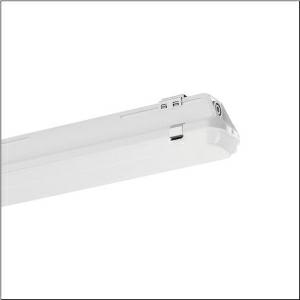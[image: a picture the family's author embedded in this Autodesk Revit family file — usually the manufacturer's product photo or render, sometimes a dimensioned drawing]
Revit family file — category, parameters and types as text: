
# Revit family: monsun_11_51fp20ep460l
name_source: partatom
category: Lighting Fixtures
units: mm (PartAtom-declared; Revit-internal decimal feet)

## family parameters
Cut with Voids When Loaded = No
Host = Face
Light Source = No
Part Type = Normal
Room Calculation Point = No
Round Connector Dimension = Use Diameter
Shared = No

## types (1)
- --- (1 x LED, 5450 lm, 31.5 W, 4000K)
    Apparent Load = 32 VA
    CIE Flux Codes = 45 75 93 94 100
    Color Rendering = 80
    Color Temperature = 4000K
    Default Elevation = 1800 mm
    Description = Monsun 11, damp-proof luminaire, chain hanger, primary optical cover: enclosure, of PC, light emission: direct distribution, primary light characteristic: symmetric, installation type: suspended mounting, surface-mounted, horizontal mounting, vertical mounting, LED, rated luminous flux: 5.450lm, luminous efficacy: 173lm/W, light colour: 840, colour temperature: 4000K, control gear: DALI 2, with terminal, 5-pole, max. 2.5mm², mains connection: 220..240V, AC, 50/60Hz, rated input power: 32W, luminaire housing, of glass-fibre reinforced polyester, uncoated, bright grey, incl. chain hanger, length: 1.590mm, width: 90mm, height: 88mm, clip for enclosure, of stainless steel (V2A), ceiling mounting element, of stainless steel (V2A), chain hanger, of stainless steel (V2A), protection rating (complete): IP66, insulation class (complete): insulation class I (protective earthing), certification: CE, ENEC, VDE, UKCA, protection symbol: D, impact resistance: IK08, permissible operating ambient temperature: -25..+35°C, standard: EN 50419, EN 60598-2-1, corresponds to IFS (International Featured Standards) requirements for safety and quality in the food industry, for indoor or canopied outdoor use, no direct snow, no direct sun, no direct rain, LABS conformity tested according to VDMA 24364:2018-05, contact your sales advisor before using the luminaires in applications with unclear chemical exposure, large temperature fluctuations or condensation-forming humidity, packaging unit: 1 piece
    Height = 89 mm
    Lamp = 1 x LED
    Lamp Light Flux = 5450 lm
    Lamp Power = 31.5 W
    Lamp count = 1
    Length = 1590 mm
    Luminous efficacy = 173 lm/W
    Manufacturer = Siteco
    ModVariant = No
    Model = 51FP20EP460L
    Mounting Place = Ceiling
    Mounting Type = Surface mounted
    Number of Poles = 1
    OnlyDefault = Yes
    Power Factor = 1
    Product Name = Monsun 11
    Product group = damp-proof luminaire
    ProductGroupID = 300
    Protection Class = Protection class I
    Protection Degree = IP 66
    RLX_Detail_Level = 1
    RLX_Emergency_Light_Flux = 0 lm
    RLX_Emergency_Type = 0
    RLX_Emergency_Type_DB = No
    RlxData = <blob elided: 92049 chars, md5=b080c202>
    Socket = socket
    Standby Power = 0 W
    System Light Flux = 5450 lm
    System Power = 32 W
    Type Comments = factory setting: luminous flux: 100 % | dim-lin: 254 | 219 mA
    Type Image = l_1349237.jpg
    URL = http://relux.com
    VarID = @adj_034119
    Voltage = 0 V
    Weight = 0.00 kg
    Width = 90 mm

## geometry (parser evidence)
native form markers: Blend x4, Sweep x12
no freeform markers — native parametric forms only
